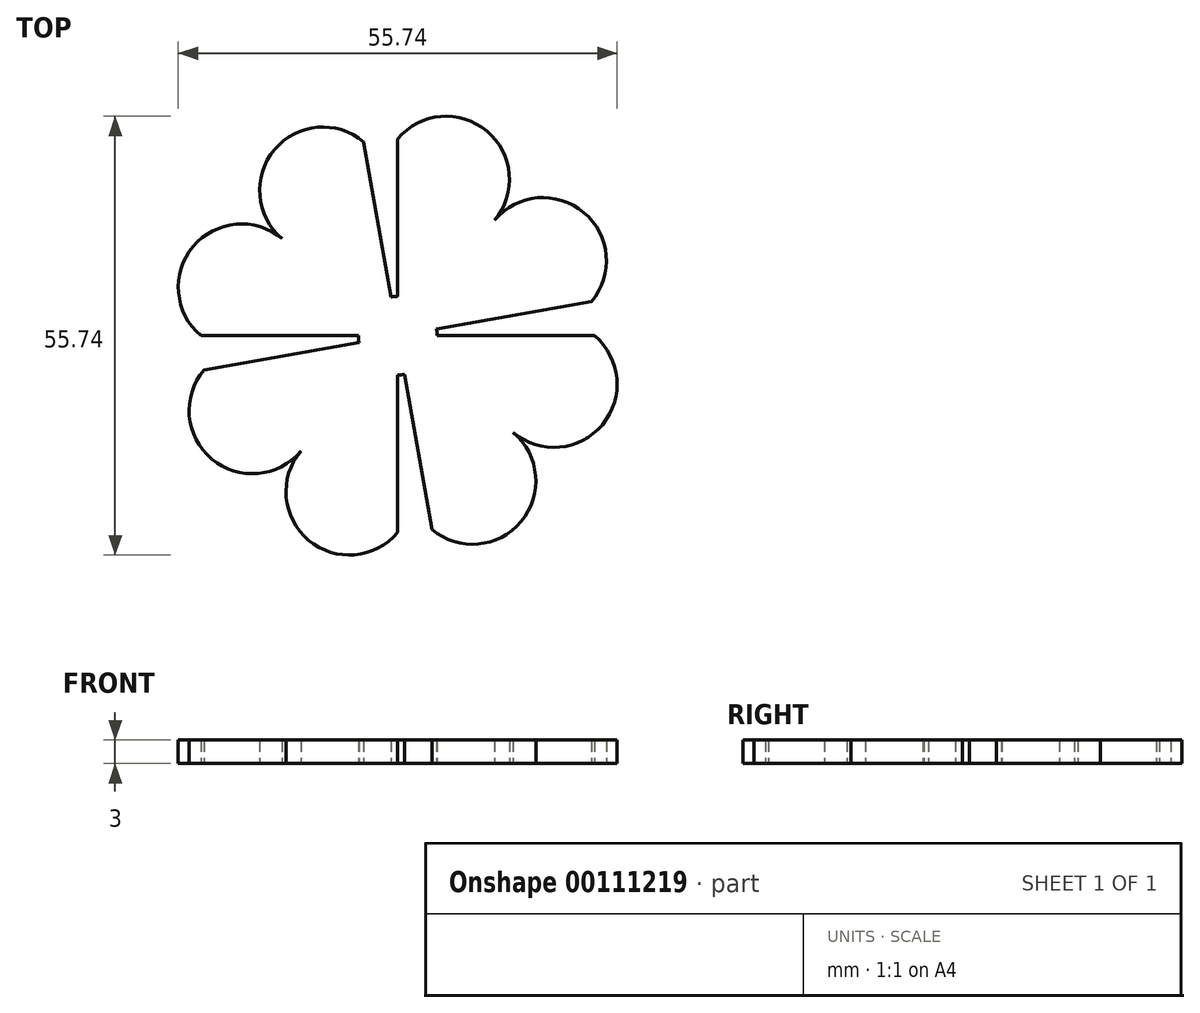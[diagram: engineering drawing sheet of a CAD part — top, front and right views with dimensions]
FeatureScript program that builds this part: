
annotation { "Feature Type Name" : "Feature", "Feature Type Description" : "" }
export const myFeature = defineFeature(function(context is Context, id is Id, definition is map)
    precondition{}
    {
        {
            var Q0;
            Q0=qCreatedBy(makeId("Top.planeOp"),FACE);
            var sketch = newSketch(context, id + "F0", { "sketchPlane" : qUnion([Q0])});
            skLineSegment(sketch, "E0", {"start": v(0, 0) * mm, "end": v(24.62, 4.34) * mm});
            skLineSegment(sketch, "E1", {"start": v(24.62, 4.34) * mm, "end": v(0, 25) * mm, "construction": true});
            skLineSegment(sketch, "E2", {"start": v(0, 25) * mm, "end": v(0, 0) * mm});
            skArc(sketch, "E3", {"start": v(12.31, 14.67) * mm, "mid": v(11.32, 26) * mm, "end": v(0, 25) * mm});
            skArc(sketch, "E4", {"start": v(24.62, 4.34) * mm, "mid": v(23.63, 15.66) * mm, "end": v(12.31, 14.67) * mm});
            skSolve(sketch);
        }
        {
            var Q0;
            Q0 = qSketchRegion(id + "F0", true);
            extrude(context, id + "F1", {"entities" : qUnion([Q0]), "depth" : 3 * mm});
        }
        {
            var Q0;
            Q0=makeQuery(id+"F1.opExtrude","SWEPT_BODY",BODY,{"disambiguationData":[OSD([sQuery(id+"F0.wireOp",EDGE,"E0"),sQuery(id+"F0.wireOp",EDGE,"E2"),sQuery(id+"F0.wireOp",EDGE,"E3"),sQuery(id+"F0.wireOp",EDGE,"E4")])]});
            var Q1;
            Q1=makeQuery(id+"F1.opExtrude","SWEPT_EDGE",EDGE,{"disambiguationData":[OSD([sQuery(id+"F0.wireOp",EDGE,"E0"),sQuery(id+"F0.wireOp",EDGE,"E2")])]});
            circularPattern(context, id + "F2", {"entities" : qUnion([Q0]), "axis" : qUnion([Q1]), "angle" : 90 * degree, "instanceCount" : 4});
        }
        {
            var Q0;
            Q0=qCreatedBy(makeId("Top.planeOp"),FACE);
            var sketch = newSketch(context, id + "F3", { "sketchPlane" : qUnion([Q0])});
            skCircle(sketch, "E5", {"center": v(0, 0) * mm, "radius": 5 * mm});
            skSolve(sketch);
        }
        {
            var Q0;
            Q0 = qSketchRegion(id + "F3", true);
            extrude(context, id + "F4", {"entities" : qUnion([Q0]), "operationType" : NewBodyOperationType.ADD, "depth" : 3 * mm});
        }
    });
